FCSTD DOCUMENT  (FreeCAD 0.20R27319 (Git))
Label: Protractor
License: All rights reserved
LicenseURL: http://en.wikipedia.org/wiki/All_rights_reserved
objects: Part::Part2DObjectPython×22, Part::FeaturePython×3
note: 22 computed .brp shape members not serialized (recipe doc carries the construction recipe); baked Part::Feature solids carry a one-line shape summary decoded from their .brp

FEATURE [Part::Part2DObjectPython] Line  # Draft 2D object (typed FeaturePython)
  Area = 0
  ChamferSize = 0
  Closed = true
  End = (-500,100,0)
  FilletRadius = 0
  Length = 25
  MakeFace = false
  Placement = pos=(0,40.368,0) rot=(0,0,1;0rad)
  Points = (2) [(-500,34.632,0),(-500,59.632,0)]
  Start = (-500,75,0)
  Subdivisions = 0
FEATURE [Part::FeaturePython] Array  # Draft array (typed FeaturePython)
  AlwaysSyncPlacement = false
  Angle = -50
  ArrayType = 1
  Axis = (0,0,1)
  Base = -> Line
  Center = (-500,-500,0)
  Count = 11
  ExpandArray = false
  Fuse = false
  IntervalAxis = (0,0,0)
  IntervalX = (50,0,0)
  IntervalY = (0,50,0)
  IntervalZ = (0,0,50)
  NumberCircles = 3
  NumberPolar = 11
  NumberX = 2
  NumberY = 2
  NumberZ = 1
  PlacementList = 11 placements: [(0,40.368,0),(45.1935,-5.26613,0),(86.2378,-54.6655,0),(122.82,-107.454,0),(154.663,-163.23,0),(181.523,-221.569,0),(203.197,-282.028,0),(219.518,-344.145,0),(230.364,-407.448,0),(235.651,-471.456,0),(235.34,-535.68,0)]
  RadialDistance = 50
  ScaleList = (11) [(1,1,1),(1,1,1),(1,1,1),(1,1,1),(1,1,1),(1,1,1),(1,1,1),(1,1,1),(1,1,1),(1,1,1),(1,1,1)]
  Symmetry = 1
  TangentialDistance = 25
FEATURE [Part::Part2DObjectPython] Line001  # Draft 2D object (typed FeaturePython)
  Area = 0
  ChamferSize = 0
  Closed = true
  End = (-500,75,0)
  FilletRadius = 0
  Length = 25
  MakeFace = false
  Placement = pos=(-48.9929,29.9523,0) rot=(0,0,1;0rad)
  Points = (2) [(-451.007,20.0477,0),(-451.007,45.0477,0)]
  Start = (-500,50,0)
  Subdivisions = 0
FEATURE [Part::FeaturePython] Array001  # Draft array (typed FeaturePython)
  AlwaysSyncPlacement = false
  Angle = -50
  ArrayType = 1
  Axis = (0,0,1)
  Base = -> Line001
  Center = (-500,-500,0)
  Count = 51
  ExpandArray = false
  Fuse = false
  IntervalAxis = (0,0,0)
  IntervalX = (50,0,0)
  IntervalY = (0,50,0)
  IntervalZ = (0,0,50)
  NumberCircles = 3
  NumberPolar = 51
  NumberX = 2
  NumberY = 2
  NumberZ = 1
  PlacementList = 51 placements: [(-48.9929,29.9523,0),(-39.8126,22.0004,0),(-30.7725,13.8895,0),(-21.8754,5.62211,0),(-13.1239,-2.79933,0),(-4.5207,-11.3722,0),(3.93156,-20.0939,0),(12.2303,-28.9618,0),(20.3731,-37.9732,0),(28.3573,-47.1254,0),(36.1806,-56.4155,0),(43.8405,-65.8407,0),(51.3348,-75.3981,0),(58.6612,-85.0849,0),(65.8174,-94.8981,0),(72.8012,-104.835,0),(79.6105,-114.892,0),(86.2433,-125.066,0),(92.6975,-135.354,0),+32 more]
  RadialDistance = 50
  ScaleList = (51) [(1,1,1),(1,1,1),(1,1,1),(1,1,1),(1,1,1),(1,1,1),(1,1,1),(1,1,1),(1,1,1),(1,1,1),(1,1,1),(1,1,1),(1,1,1),(1,1,1),(1,1,1),(1,1,1),(1,1,1),(1,1,1),+33 more]
  Symmetry = 1
  TangentialDistance = 25
FEATURE [Part::Part2DObjectPython] Line002  # Draft 2D object (typed FeaturePython)
  Area = 0
  ChamferSize = 0
  Closed = false
  End = (-500,-550,0)
  FilletRadius = 0
  Length = 100
  MakeFace = false
  Placement = pos=(-499.804,-460.608,0) rot=(0,0,1;0rad)
  Points = (2) [(-0.195679,10.6083,0),(-0.195679,-89.3917,0)]
  Start = (-500,-450,0)
  Subdivisions = 0
FEATURE [Part::Part2DObjectPython] Line003  # Draft 2D object (typed FeaturePython)
  Area = 0
  ChamferSize = 0
  Closed = false
  End = (-450,-500,0)
  FilletRadius = 0
  Length = 100
  MakeFace = false
  Placement = pos=(-533.788,-500.256,0) rot=(0,0,1;0rad)
  Points = (2) [(-16.2123,0.255524,0),(83.7877,0.255524,0)]
  Start = (-550,-500,0)
  Subdivisions = 0
FEATURE [Part::Part2DObjectPython] Circle  # Draft 2D object (typed FeaturePython)
  Area = 0
  FirstAngle = 0
  LastAngle = 0
  MakeFace = false
  Placement = pos=(-500,-500,0) rot=(0,0,1;0rad)
  Radius = 5
FEATURE [Part::Part2DObjectPython] Arc  # Draft 2D object (typed FeaturePython)
  Area = 0
  FirstAngle = 35
  LastAngle = 95
  MakeFace = false
  Placement = pos=(-500,-500,0) rot=(0,0,1;0rad)
  Radius = 490
FEATURE [Part::Part2DObjectPython] Rectangle  # Draft 2D object (typed FeaturePython)
  Area = 0
  ChamferSize = 0
  Columns = 1
  FilletRadius = 0
  Height = 800
  Length = 800
  MakeFace = false
  Placement = pos=(-600,-600,0) rot=(0,0,1;0rad)
  Rows = 1
FEATURE [Part::Part2DObjectPython] ShapeString001  label="ShapeString-001"  # Draft 2D object (typed FeaturePython)
  FontFile = <path>
  MakeFace = true
  Placement = pos=(-510,120,0) rot=(0,0,-1;1.5708rad)
  Size = 20
  String = 0
  Tracking = 0
FEATURE [Part::Part2DObjectPython] ShapeString002  label="ShapeString-002"  # Draft 2D object (typed FeaturePython)
  FontFile = <path>
  MakeFace = true
  Placement = pos=(-455,118,0) rot=(0,0,-1;1.65806rad)
  Size = 20
  String = 5
  Tracking = 0
FEATURE [Part::Part2DObjectPython] ShapeString003  label="ShapeString-003"  # Draft 2D object (typed FeaturePython)
  FontFile = <path>
  MakeFace = true
  Placement = pos=(-398,129,0) rot=(0,0,-1;1.74533rad)
  Size = 20
  String = 10
  Tracking = 0
FEATURE [Part::Part2DObjectPython] ShapeString004  label="ShapeString-004"  # Draft 2D object (typed FeaturePython)
  FontFile = <path>
  MakeFace = true
  Placement = pos=(-343,117,0) rot=(0,0,-1;1.8326rad)
  Size = 20
  String = 15
  Tracking = 0
FEATURE [Part::Part2DObjectPython] ShapeString005  label="ShapeString-005"  # Draft 2D object (typed FeaturePython)
  FontFile = <path>
  MakeFace = true
  Placement = pos=(-290,101,0) rot=(0,0,-1;1.91986rad)
  Size = 20
  String = 20
  Tracking = 0
FEATURE [Part::Part2DObjectPython] ShapeString006  label="ShapeString-006"  # Draft 2D object (typed FeaturePython)
  FontFile = <path>
  MakeFace = true
  Placement = pos=(-240,82,0) rot=(0,0,1;-2.00713rad)
  Size = 20
  String = 25
  Tracking = 0
FEATURE [Part::Part2DObjectPython] ShapeString007  label="ShapeString-007"  # Draft 2D object (typed FeaturePython)
  FontFile = <path>
  MakeFace = true
  Placement = pos=(-189,56,0) rot=(0,0,-1;2.0944rad)
  Size = 20
  String = 30
  Tracking = 0
FEATURE [Part::Part2DObjectPython] ShapeString008  label="ShapeString-008"  # Draft 2D object (typed FeaturePython)
  FontFile = <path>
  MakeFace = true
  Placement = pos=(-144,26,0) rot=(0,0,1;4.10152rad)
  Size = 20
  String = 35
  Tracking = 0
FEATURE [Part::Part2DObjectPython] ShapeString009  label="ShapeString-009"  # Draft 2D object (typed FeaturePython)
  FontFile = <path>
  MakeFace = true
  Placement = pos=(-99,-6,0) rot=(0,0,1;4.01426rad)
  Size = 20
  String = 40
  Tracking = 0
FEATURE [Part::Part2DObjectPython] ShapeString010  label="ShapeString-010"  # Draft 2D object (typed FeaturePython)
  FontFile = <path>
  MakeFace = true
  Placement = pos=(-57,-44,0) rot=(0,0,1;3.92699rad)
  Size = 20
  String = 45
  Tracking = 0
FEATURE [Part::Part2DObjectPython] ShapeString011  label="ShapeString-011"  # Draft 2D object (typed FeaturePython)
  FontFile = <path>
  MakeFace = true
  Placement = pos=(-18,-84,0) rot=(0,0,1;3.83972rad)
  Size = 20
  String = 50
  Tracking = 0
FEATURE [Part::Part2DObjectPython] Line004  # Draft 2D object (typed FeaturePython)
  Area = 0
  ChamferSize = 0
  Closed = false
  End = (-500,0,0)
  FilletRadius = 0
  Length = 50
  MakeFace = false
  Placement = pos=(-500.448,23.4823,0) rot=(0,0,1;0rad)
  Points = (2) [(0.447815,26.5177,0),(0.447815,-23.4823,0)]
  Start = (-500,50,0)
  Subdivisions = 0
FEATURE [Part::FeaturePython] Array002  # Draft array (typed FeaturePython)
  AlwaysSyncPlacement = false
  Angle = -50
  ArrayType = 1
  Axis = (0,0,1)
  Base = -> Line004
  Center = (-500,-500,0)
  Count = 101
  ExpandArray = false
  Fuse = false
  IntervalAxis = (0,0,0)
  IntervalX = (50,0,0)
  IntervalY = (0,50,0)
  IntervalZ = (0,0,50)
  NumberCircles = 3
  NumberPolar = 101
  NumberX = 2
  NumberY = 2
  NumberZ = 1
  PlacementList = 101 placements: [(-500.448,23.4823,0),(-495.88,23.4663,0),(-491.312,23.4104,0),(-486.744,23.3146,0),(-482.178,23.179,0),(-477.613,23.0036,0),(-473.05,22.7883,0),(-468.489,22.5332,0),(-463.93,22.2384,0),(-459.374,21.9037,0),(-454.822,21.5293,0),(-450.272,21.1152,0),(-445.727,20.6614,0),(-441.185,20.168,0),(-436.648,19.6349,0),(-432.116,19.0623,0),(-427.589,18.4501,0),(-423.067,17.7985,0),(-418.552,17.1074,0),+82 more]
  RadialDistance = 50
  ScaleList = (101) [(1,1,1),(1,1,1),(1,1,1),(1,1,1),(1,1,1),(1,1,1),(1,1,1),(1,1,1),(1,1,1),(1,1,1),(1,1,1),(1,1,1),(1,1,1),(1,1,1),(1,1,1),(1,1,1),(1,1,1),(1,1,1),+83 more]
  Symmetry = 1
  TangentialDistance = 25
FEATURE [Part::Part2DObjectPython] Arc001  # Draft 2D object (typed FeaturePython)
  Area = 0
  FirstAngle = 35
  LastAngle = 95
  MakeFace = false
  Placement = pos=(-500,-500,0) rot=(0,0,1;0rad)
  Radius = 650
FEATURE [Part::Part2DObjectPython] Line005  # Draft 2D object (typed FeaturePython)
  Area = 0
  ChamferSize = 0
  Closed = true
  End = (-556.651,147.527,0)
  FilletRadius = 0
  Length = 160
  MakeFace = false
  Placement = pos=(-500,-500,0) rot=(0,0,1;0.087266rad)
  Points = (2) [(-1.13687e-13,490,0),(-4.54747e-13,650,0)]
  Start = (-542.706,-11.8646,0)
  Subdivisions = 0
FEATURE [Part::Part2DObjectPython] Line006  # Draft 2D object (typed FeaturePython)
  Area = 0
  ChamferSize = 0
  Closed = true
  End = (32.4488,-127.175,0)
  FilletRadius = 0
  Length = 160
  MakeFace = false
  Placement = pos=(-500,-500,0) rot=(0,0,1;-0.959931rad)
  Points = (2) [(-4.26326e-14,490,0),(-4.68958e-13,650,0)]
  Start = (-98.6155,-218.948,0)
  Subdivisions = 0
note: 11 file-system paths scrubbed to <path> (originals preserved in the JSON sidecar)
